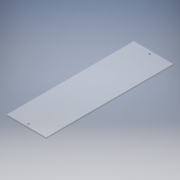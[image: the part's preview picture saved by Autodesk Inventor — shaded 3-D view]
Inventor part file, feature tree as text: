
AUTODESK INVENTOR PART (.ipt)
format: ipt  version: 2018 (Build 220112000, 112)  size: 123,392 bytes
history: native  units: mm
features: extrude x2, sketch x2
ambient origin geometry x8: Origin, YZ Plane, XZ Plane, XY Plane, X Axis, Y Axis, Z Axis, Center Point
bodies: Volumenkörper1 (feature_tree)
feature tree (4):
  extrude  "Extrusion1"  Depth=180.0mm
  extrude  "Extrusion3"  Depth=10.0mm
  sketch  "Skizze1"  dims[d0=580.0mm d1=180.0mm]
  sketch  "Sketch4"  dims[d2=6.0mm d3=0.0mm d11=7.65mm d12=93.75mm d13=14.0mm d14=7.65mm d15=14.0mm d16=93.75mm d17=10.0mm d18=0.0mm]
